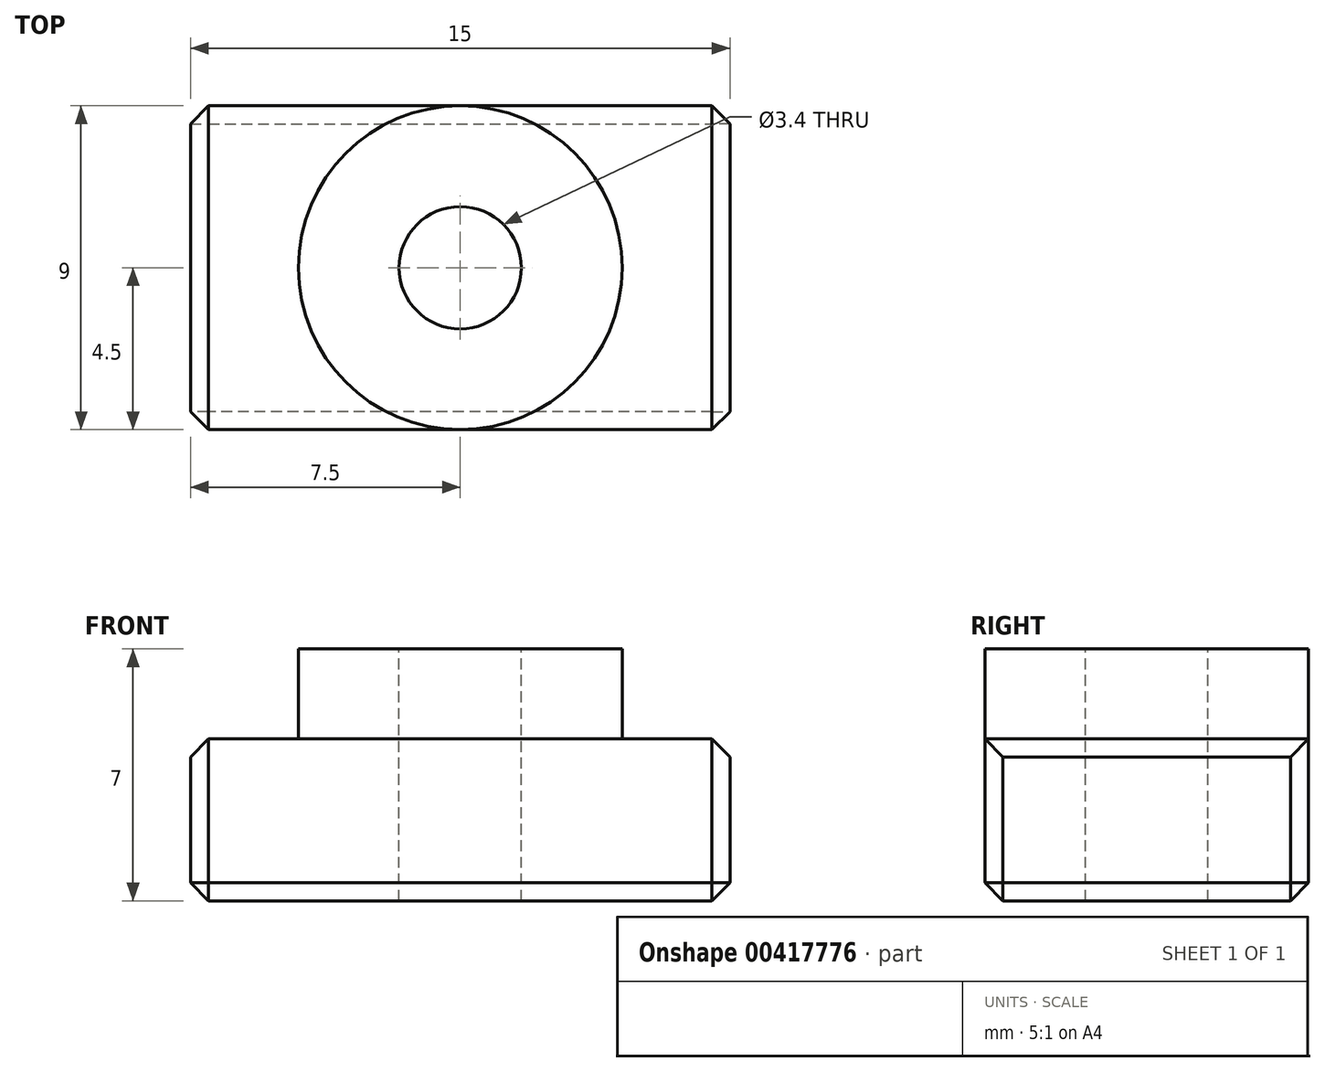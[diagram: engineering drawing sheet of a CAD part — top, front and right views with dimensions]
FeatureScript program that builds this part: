
annotation { "Feature Type Name" : "Feature", "Feature Type Description" : "" }
export const myFeature = defineFeature(function(context is Context, id is Id, definition is map)
    precondition{}
    {
        {
            var Q0;
            Q0=qCreatedBy(makeId("Top.planeOp"),FACE);
            var sketch = newSketch(context, id + "F0", { "sketchPlane" : qUnion([Q0])});
            skLineSegment(sketch, "E0.bottom", {"start": v(-7.5, 4.5) * mm, "end": v(7.5, 4.5) * mm});
            skLineSegment(sketch, "E0.top", {"start": v(-7.5, -4.5) * mm, "end": v(7.5, -4.5) * mm});
            skLineSegment(sketch, "E0.left", {"start": v(-7.5, 4.5) * mm, "end": v(-7.5, -4.5) * mm});
            skLineSegment(sketch, "E0.right", {"start": v(7.5, 4.5) * mm, "end": v(7.5, -4.5) * mm});
            skSolve(sketch);
        }
        {
            var Q0;
            Q0=makeQuery(id+"F0.imprint","IMPRINT",FACE,{"disambiguationData":[TD([[makeQuery(id+"F0.imprint","IMPRINT",EDGE,{"derivedFrom":sQuery(id+"F0.wireOp",EDGE,"E0.bottom")}),-1.0]])]});
            extrude(context, id + "F1", {"entities" : qUnion([Q0]), "depth" : 4.5 * mm});
        }
        {
            var Q0;
            Q0=makeQuery(id+"F1.opExtrude","CAP_FACE",FACE,{"disambiguationData":[OSD([sQuery(id+"F0.wireOp",EDGE,"E0.bottom"),sQuery(id+"F0.wireOp",EDGE,"E0.top"),sQuery(id+"F0.wireOp",EDGE,"E0.left"),sQuery(id+"F0.wireOp",EDGE,"E0.right")])],"isStart":false});
            var sketch = newSketch(context, id + "F2", { "sketchPlane" : qUnion([Q0])});
            skCircle(sketch, "E1", {"center": v(0, 0) * mm, "radius": 4.5 * mm});
            skSolve(sketch);
        }
        {
            var Q0;
            Q0 = qSketchRegion(id + "F2", true);
            extrude(context, id + "F3", {"entities" : qUnion([Q0]), "operationType" : NewBodyOperationType.ADD, "depth" : 2.5 * mm});
        }
        {
            var Q0;
            Q0=makeQuery(id+"F3.opExtrude","CAP_FACE",FACE,{"disambiguationData":[OSD([sQuery(id+"F2.wireOp",EDGE,"E1")])],"isStart":false});
            var sketch = newSketch(context, id + "F4", { "sketchPlane" : qUnion([Q0])});
            skCircle(sketch, "E2", {"center": v(0, 0) * mm, "radius": 1.7 * mm});
            skSolve(sketch);
        }
        {
            var Q0;
            Q0 = qSketchRegion(id + "F4", true);
            extrude(context, id + "F5", {"entities" : qUnion([Q0]), "operationType" : NewBodyOperationType.REMOVE, "endBound" : BoundingType.THROUGH_ALL, "oppositeDirection" : true, "depth" : 25 * mm});
        }
        {
            var Q0;
            Q0=makeQuery(id+"F1.opExtrude","CAP_EDGE",EDGE,{"disambiguationData":[OSD([sQuery(id+"F0.wireOp",EDGE,"E0.left")])],"isStart":false});
            var Q1;
            Q1=makeQuery(id+"F1.opExtrude","CAP_EDGE",EDGE,{"disambiguationData":[OSD([sQuery(id+"F0.wireOp",EDGE,"E0.right")])],"isStart":false});
            var Q2;
            Q2=makeQuery(id+"F1.opExtrude","SWEPT_EDGE",EDGE,{"disambiguationData":[OSD([sQuery(id+"F0.wireOp",EDGE,"E0.top"),sQuery(id+"F0.wireOp",EDGE,"E0.left")])]});
            var Q3;
            Q3=makeQuery(id+"F1.opExtrude","SWEPT_EDGE",EDGE,{"disambiguationData":[OSD([sQuery(id+"F0.wireOp",EDGE,"E0.bottom"),sQuery(id+"F0.wireOp",EDGE,"E0.left")])]});
            var Q4;
            Q4=makeQuery(id+"F1.opExtrude","SWEPT_EDGE",EDGE,{"disambiguationData":[OSD([sQuery(id+"F0.wireOp",EDGE,"E0.top"),sQuery(id+"F0.wireOp",EDGE,"E0.right")])]});
            var Q5;
            Q5=makeQuery(id+"F1.opExtrude","SWEPT_EDGE",EDGE,{"disambiguationData":[OSD([sQuery(id+"F0.wireOp",EDGE,"E0.bottom"),sQuery(id+"F0.wireOp",EDGE,"E0.right")])]});
            var Q6;
            Q6=makeQuery(id+"F1.opExtrude","CAP_EDGE",EDGE,{"disambiguationData":[OSD([sQuery(id+"F0.wireOp",EDGE,"E0.bottom")])],"isStart":true});
            var Q7;
            Q7=makeQuery(id+"F1.opExtrude","CAP_EDGE",EDGE,{"disambiguationData":[OSD([sQuery(id+"F0.wireOp",EDGE,"E0.right")])],"isStart":true});
            var Q8;
            Q8=makeQuery(id+"F1.opExtrude","CAP_EDGE",EDGE,{"disambiguationData":[OSD([sQuery(id+"F0.wireOp",EDGE,"E0.top")])],"isStart":true});
            var Q9;
            Q9=makeQuery(id+"F1.opExtrude","CAP_EDGE",EDGE,{"disambiguationData":[OSD([sQuery(id+"F0.wireOp",EDGE,"E0.left")])],"isStart":true});
            chamfer(context, id + "F6", {"entities" : qUnion([Q0, Q1, Q2, Q3, Q4, Q5, Q6, Q7, Q8, Q9]), "width" : 0.5 * mm, "tangentPropagation" : true});
        }
    });
